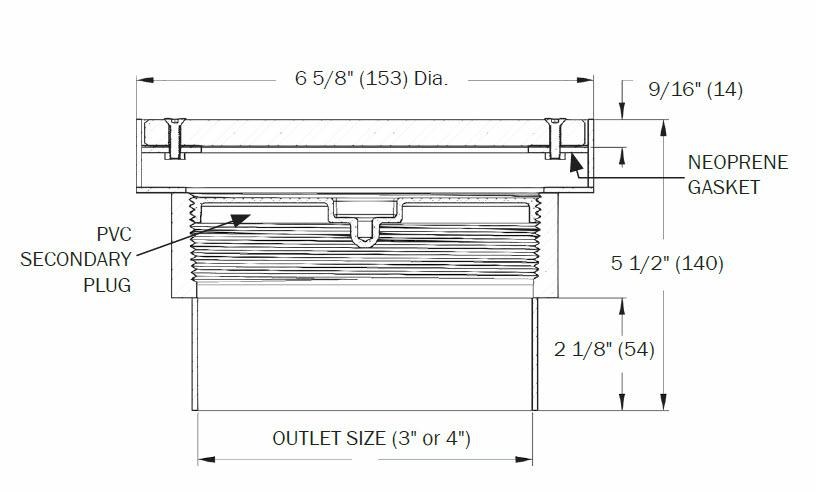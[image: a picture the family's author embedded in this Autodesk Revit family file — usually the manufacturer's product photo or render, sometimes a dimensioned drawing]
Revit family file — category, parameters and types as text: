
# Revit family: P7080
name_source: partatom
category: Plumbing Fixtures
revit_build: Autodesk Revit 2018 (Build: 20170223_1515(x64)
units: mm (PartAtom-declared; Revit-internal decimal feet)

## family parameters
Cut with Voids When Loaded = No
Host = Face
Part Type = Normal
Room Calculation Point = No
Round Connector Dimension = Use Radius
Shared = No

## types (3) — shared parameters
Default Elevation = 0' - 0"
Description = 8" ROUND, TYPE 316 STAINLESS STEEL FABRICATED FLOOR CLEANOUT
Floor Drain Material = Paint - Sherwin Williams Paint - #952C2A - Bellwood Red
MH-501 = No
MH-600 = No
Manufacturer = MIFAB
URL = WWW.MIFAB.COM
zero-valued in all types: CWFU, WFU

## per-type parameters (varying)
| type | MH-301 | MH-401 | Model | Pipe Diameter | Pipe Radius |
| P7083_Ø3" | Yes | No | P7083 | 0' - 3" | 0' - 1 1/2" |
| P7084_Ø4" | No | Yes | P7084 | 0' - 4" | 0' - 2" |
| P7086_Ø6" | No | Yes | P7086 | 0' - 6" | 0' - 3" |

## geometry (parser evidence)
native form markers: Sweep x6
no freeform markers — native parametric forms only
